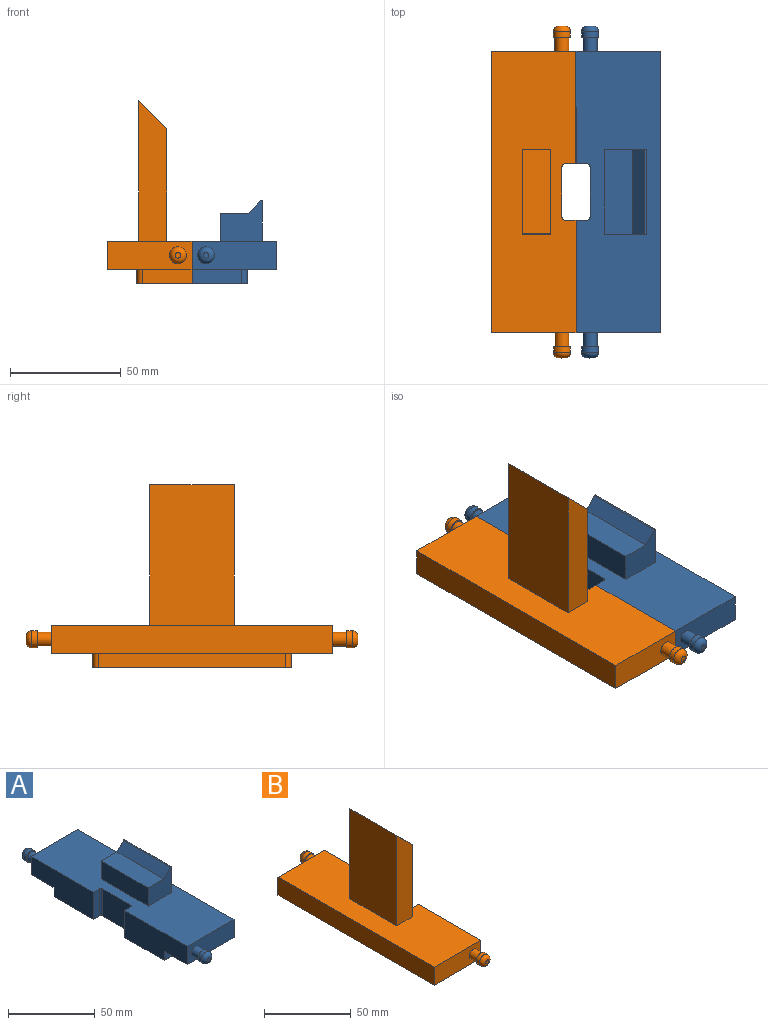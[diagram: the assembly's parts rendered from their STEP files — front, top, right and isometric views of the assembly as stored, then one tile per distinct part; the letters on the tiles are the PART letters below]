
ASSEMBLY  parts=2 mates=1
PART A: 35 faces, bbox 38.1x149.9x37.4 mm
  f0: plane 127x38.1mm, normal (0,0,1), area 3952.3mm2, adj f6,f7,f8,f11,f12,f13,f14,f15
  f1: plane 22.35x6.35mm, normal (0,-1,0), area 141.9mm2, adj f3,f4,f9,f17
  f2: plane 22.35x6.35mm, normal (0,1,0), area 141.9mm2, adj f3,f4,f10,f16
  f3: plane 89.66x24.89mm, normal (0,0,-1), area 2068.5mm2, adj f1,f2,f5,f6,f7,f8,f9,f10
  f4: plane 127x38.1mm, normal (0,0,-1), area 2609.6mm2, adj f1,f2,f5,f9,f10,f11,f12,f13
  f5: plane 84.58x6.35mm, normal (1,0,0), area 537.1mm2, adj f3,f4,f9,f10
  f6: plane 22.86x19.05mm, normal (-1,0,0), area 435.5mm2, adj f0,f3,f14,f15
  f7: plane 19.05x5.08mm, normal (0,1,0), area 96.8mm2, adj f0,f3,f14,f17
  f8: plane 19.05x5.08mm, normal (0,-1,0), area 96.8mm2, adj f0,f3,f15,f16
  f9: cylinder r=2.54mm len=6.35mm, axis (0,0,1), area 25.3mm2, adj f1,f3,f4,f5
  f10: cylinder r=2.54mm len=6.35mm, axis (0,0,-1), area 25.3mm2, adj f2,f3,f4,f5
  f11: plane 38.1x12.7mm, normal (0,-1,0), area 452.2mm2, adj f0,f4,f12,f17,f18
  f12: plane 127x12.7mm, normal (1,0,0), area 1612.9mm2, adj f0,f4,f11,f13
  f13: plane 38.1x12.7mm, normal (0,1,0), area 452.2mm2, adj f0,f4,f12,f16,f23
  f14: cylinder r=1.27mm len=19.05mm, axis (0,0,-1), area 38mm2, adj f0,f3,f6,f7
  f15: cylinder r=1.27mm len=19.05mm, axis (0,0,1), area 38mm2, adj f0,f3,f6,f8
  f16: plane 50.8x19.05mm, normal (-1,0,0), area 849.2mm2, adj f0,f2,f3,f4,f8,f13
  f17: plane 50.8x19.05mm, normal (-1,0,0), area 849.2mm2, adj f0,f1,f3,f4,f7,f11
  f18: cylinder r=3.17mm len=6.35mm, axis (0,1,0), area 126.7mm2, adj f11,f21
  f19: cylinder r=3.81mm len=7.62mm, axis (0,1,0), area 60.8mm2, adj f21,f22
  f20: plane 2.54x2.54mm, normal (0,-1,0), area 5.1mm2, adj f22
  f21: plane 7.62x7.62mm, normal (0,1,0), area 13.9mm2, adj f18,f19
  f22: torus R=1.27mm, axis (0,-1,0), area 72.4mm2, adj f19,f20
  f23: cylinder r=3.17mm len=6.35mm, axis (0,-1,0), area 126.7mm2, adj f13,f26
  f24: cylinder r=3.81mm len=7.62mm, axis (0,-1,0), area 60.8mm2, adj f26,f27
  f25: plane 2.54x2.54mm, normal (0,1,0), area 5.1mm2, adj f27
  f26: plane 7.62x7.62mm, normal (0,-1,0), area 13.9mm2, adj f23,f24
  f27: torus R=1.27mm, axis (0,1,0), area 72.4mm2, adj f24,f25
  f28: plane 38.1x12.7mm, normal (-1,0,0), area 483.9mm2, adj f0,f29,f30,f31
  f29: plane 19.05x18.33mm, normal (0,-1,0), area 261.8mm2, adj f0,f28,f31,f32,f33,f34
  f30: plane 19.05x18.33mm, normal (0,1,0), area 261.8mm2, adj f0,f28,f31,f32,f33,f34
  f31: plane 38.1x12.7mm, normal (0,0,1), area 483.9mm2, adj f28,f29,f30,f33
  f32: plane 38.1x17.82mm, normal (1,0,0), area 679.1mm2, adj f0,f29,f30,f34
  f33: plane 38.1x5.48mm, normal (-0.71,0,0.71), area 295.4mm2, adj f29,f30,f31,f34
  f34: cylinder r=0.51mm len=38.1mm, axis (0,1,0), area 45.6mm2, adj f29,f30,f32,f33
PART B: 33 faces, bbox 38.1x149.9x82.6 mm
  f0: plane 127x38.1mm, normal (0,0,1), area 4194.2mm2, adj f1,f2,f3,f4,f7,f13,f14,f15
  f1: plane 38.1x12.7mm, normal (0,-1,0), area 452.2mm2, adj f0,f12,f13,f17,f18
  f2: plane 38.1x12.7mm, normal (0,1,0), area 452.2mm2, adj f0,f12,f13,f16,f23
  f3: plane 19.05x5.08mm, normal (0,1,0), area 96.8mm2, adj f0,f9,f14,f17
  f4: plane 19.05x5.08mm, normal (0,-1,0), area 96.8mm2, adj f0,f9,f15,f16
  f5: plane 22.35x6.35mm, normal (0,-1,0), area 141.9mm2, adj f9,f11,f12,f17
  f6: plane 22.35x6.35mm, normal (0,1,0), area 141.9mm2, adj f9,f10,f12,f16
  f7: plane 22.86x19.05mm, normal (1,0,0), area 435.5mm2, adj f0,f9,f14,f15
  f8: plane 84.58x6.35mm, normal (-1,0,0), area 537.1mm2, adj f9,f10,f11,f12
  f9: plane 89.66x24.89mm, normal (0,0,-1), area 2068.5mm2, adj f3,f4,f5,f6,f7,f8,f10,f11
  f10: cylinder r=2.54mm len=6.35mm, axis (0,0,1), area 25.3mm2, adj f6,f8,f9,f12
  f11: cylinder r=2.54mm len=6.35mm, axis (0,0,-1), area 25.3mm2, adj f5,f8,f9,f12
  f12: plane 127x38.1mm, normal (0,0,-1), area 2609.6mm2, adj f1,f2,f5,f6,f8,f10,f11,f13
  f13: plane 127x12.7mm, normal (-1,0,0), area 1612.9mm2, adj f0,f1,f2,f12
  f14: cylinder r=1.27mm len=19.05mm, axis (0,0,1), area 38mm2, adj f0,f3,f7,f9
  f15: cylinder r=1.27mm len=19.05mm, axis (0,0,-1), area 38mm2, adj f0,f4,f7,f9
  f16: plane 50.8x19.05mm, normal (1,0,0), area 849.2mm2, adj f0,f2,f4,f6,f9,f12
  f17: plane 50.8x19.05mm, normal (1,0,0), area 849.2mm2, adj f0,f1,f3,f5,f9,f12
  f18: cylinder r=3.17mm len=6.35mm, axis (0,1,0), area 126.7mm2, adj f1,f21
  f19: cylinder r=3.81mm len=7.62mm, axis (0,1,0), area 60.8mm2, adj f21,f22
  f20: plane 2.54x2.54mm, normal (0,-1,0), area 5.1mm2, adj f22
  f21: plane 7.62x7.62mm, normal (0,1,0), area 13.9mm2, adj f18,f19
  f22: torus R=1.27mm, axis (0,-1,0), area 72.4mm2, adj f19,f20
  f23: cylinder r=3.17mm len=6.35mm, axis (0,-1,0), area 126.7mm2, adj f2,f26
  f24: cylinder r=3.81mm len=7.62mm, axis (0,-1,0), area 60.8mm2, adj f26,f27
  f25: plane 2.54x2.54mm, normal (0,1,0), area 5.1mm2, adj f27
  f26: plane 7.62x7.62mm, normal (0,-1,0), area 13.9mm2, adj f23,f24
  f27: torus R=1.27mm, axis (0,1,0), area 72.4mm2, adj f24,f25
  f28: plane 63.5x12.7mm, normal (0,-1,0), area 725.8mm2, adj f0,f29,f31,f32
  f29: plane 50.8x38.1mm, normal (1,0,0), area 1935.5mm2, adj f0,f28,f30,f32
  f30: plane 63.5x12.7mm, normal (0,1,0), area 725.8mm2, adj f0,f29,f31,f32
  f31: plane 63.5x38.1mm, normal (-1,0,0), area 2419.3mm2, adj f0,f28,f30,f32
  f32: plane 38.1x12.7mm, normal (0.71,0,0.71), area 684.3mm2, adj f28,f29,f30,f31
PLACE A t=(0.5,1.78,-12.53)mm
PLACE B t=(0.5,1.78,-12.53)mm
MATE fastened B.f17 <-> A.f17  axis (1,0,0) through (0.5,-34.08,-2.12)mm
